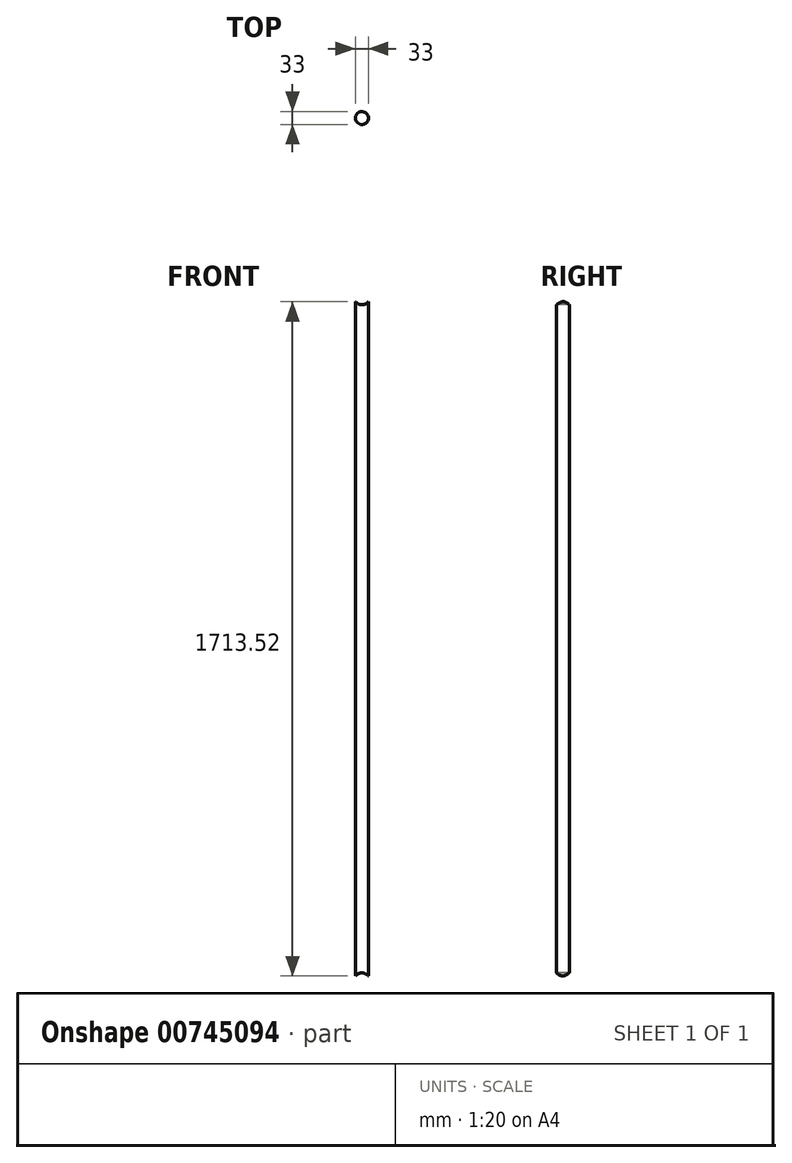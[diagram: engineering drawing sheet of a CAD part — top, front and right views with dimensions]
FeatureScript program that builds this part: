
annotation { "Feature Type Name" : "Feature", "Feature Type Description" : "" }
export const myFeature = defineFeature(function(context is Context, id is Id, definition is map)
    precondition{}
    {
        {
            var Q0;
            Q0=qCreatedBy(makeId("Top.planeOp"),FACE);
            var sketch = newSketch(context, id + "F0", { "sketchPlane" : qUnion([Q0])});
            skCircle(sketch, "E0", {"center": v(0, 0) * mm, "radius": 16.5 * mm});
            skSolve(sketch);
        }
        {
            var Q0;
            Q0=makeQuery(id+"F0.imprint","IMPRINT",FACE,{"disambiguationData":[TD([[makeQuery(id+"F0.imprint","IMPRINT",EDGE,{"derivedFrom":sQuery(id+"F0.wireOp",EDGE,"E0")}),1.0]])]});
            extrude(context, id + "F1", {"entities" : qUnion([Q0]), "depth" : 1739.5 * mm, "offsetDistance" : 25 * mm});
        }
        {
            var Q0;
            Q0=qCreatedBy(makeId("Front.planeOp"),FACE);
            var sketch = newSketch(context, id + "F2", { "sketchPlane" : qUnion([Q0])});
            skCircle(sketch, "E1", {"center": v(0, 0) * mm, "radius": 21 * mm});
            skCircle(sketch, "E2", {"center": v(0, 1739.5) * mm, "radius": 21 * mm});
            skSolve(sketch);
        }
        {
            var Q0;
            Q0=makeQuery(id+"F2.imprint","IMPRINT",FACE,{"disambiguationData":[TD([[makeQuery(id+"F2.imprint","IMPRINT",EDGE,{"derivedFrom":sQuery(id+"F2.wireOp",EDGE,"E1")}),1.0]])]});
            var Q1;
            Q1=makeQuery(id+"F2.imprint","IMPRINT",FACE,{"disambiguationData":[TD([[makeQuery(id+"F2.imprint","IMPRINT",EDGE,{"derivedFrom":sQuery(id+"F2.wireOp",EDGE,"E2")}),1.0]])]});
            extrude(context, id + "F3", {"entities" : qUnion([Q0, Q1]), "operationType" : NewBodyOperationType.REMOVE, "endBound" : BoundingType.SYMMETRIC, "oppositeDirection" : true, "depth" : 100 * mm, "offsetDistance" : 25 * mm});
        }
    });
